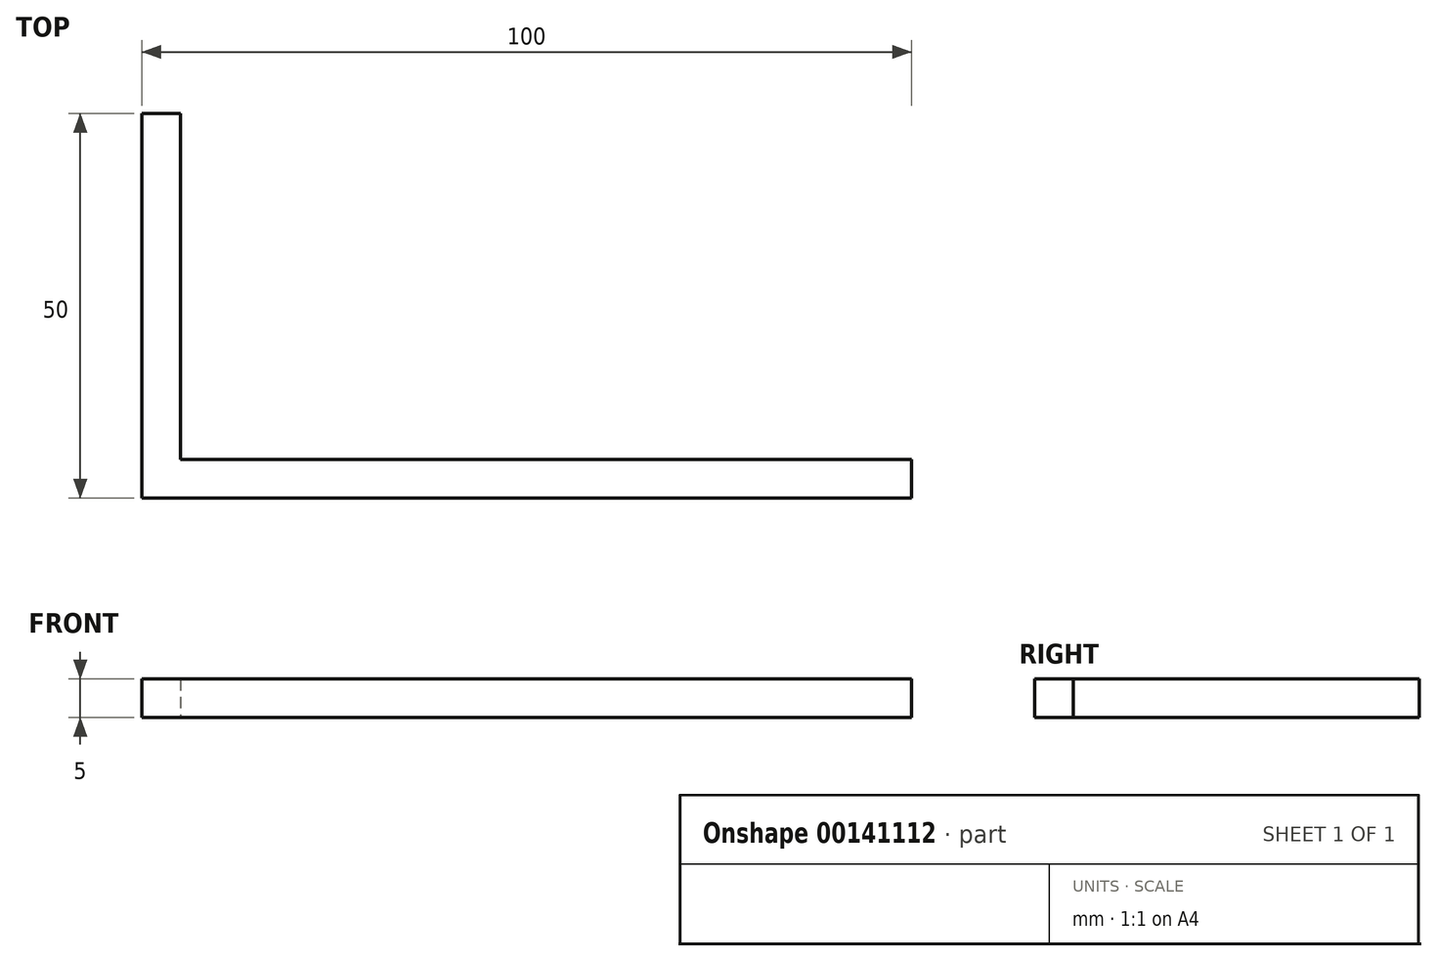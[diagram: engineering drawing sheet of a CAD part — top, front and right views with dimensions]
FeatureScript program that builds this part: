
annotation { "Feature Type Name" : "Feature", "Feature Type Description" : "" }
export const myFeature = defineFeature(function(context is Context, id is Id, definition is map)
    precondition{}
    {
        {
            var Q0;
            Q0=qCreatedBy(makeId("Top.planeOp"),FACE);
            var sketch = newSketch(context, id + "F0", { "sketchPlane" : qUnion([Q0])});
            skLineSegment(sketch, "E0.bottom", {"start": v(50, -2.5) * mm, "end": v(-50, -2.5) * mm});
            skLineSegment(sketch, "E0.top", {"start": v(50, 2.5) * mm, "end": v(-50, 2.5) * mm});
            skLineSegment(sketch, "E0.left", {"start": v(50, -2.5) * mm, "end": v(50, 2.5) * mm});
            skLineSegment(sketch, "E0.right", {"start": v(-50, -2.5) * mm, "end": v(-50, 2.5) * mm});
            skPoint(sketch, "E0.middle", {"position": v(0, 0) * mm});
            skLineSegment(sketch, "E1", {"start": v(-50, 2.5) * mm, "end": v(-50, 47.5) * mm});
            skLineSegment(sketch, "E2", {"start": v(-50, 47.5) * mm, "end": v(-45, 47.5) * mm});
            skLineSegment(sketch, "E3", {"start": v(-45, 47.5) * mm, "end": v(-45, 2.5) * mm});
            skLineSegment(sketch, "E4", {"start": v(-45, 47.5) * mm, "end": v(-45, 42.5) * mm});
            skLineSegment(sketch, "E5", {"start": v(-45, 42.5) * mm, "end": v(-50, 42.5) * mm});
            skLineSegment(sketch, "E6", {"start": v(-50, 42.5) * mm, "end": v(-50, 47.5) * mm});
            skLineSegment(sketch, "E7", {"start": v(-45, 2.5) * mm, "end": v(-45, -2.5) * mm});
            skLineSegment(sketch, "E8", {"start": v(-5, 2.5) * mm, "end": v(-5, -2.5) * mm});
            skLineSegment(sketch, "E9", {"start": v(-5, -2.5) * mm, "end": v(0, -2.5) * mm});
            skLineSegment(sketch, "E10", {"start": v(0, -2.5) * mm, "end": v(0, 2.5) * mm});
            skLineSegment(sketch, "E11", {"start": v(45, 2.5) * mm, "end": v(45, -2.5) * mm});
            skLineSegment(sketch, "E12", {"start": v(45, -2.5) * mm, "end": v(50, -2.5) * mm});
            skSolve(sketch);
        }
        {
            var Q0;
            Q0=makeQuery(id+"F0.imprint","IMPRINT",FACE,{"disambiguationData":[TD([[makeQuery(id+"F0.imprint","IMPRINT",EDGE,{"derivedFrom":sQuery(id+"F0.wireOp",EDGE,"E2")}),-1.0]])]});
            var Q1;
            {var subQ0=sQuery(id+"F0.wireOp",EDGE,"E0.right");Q1=makeQuery(id+"F0.imprint","IMPRINT",FACE,{"disambiguationData":[TD([[makeQuery(id+"F0.imprint","IMPRINT",EDGE,{"derivedFrom":subQ0}),-1.0]])]});}
            var Q2;
            {var subQ0=sQuery(id+"F0.wireOp",EDGE,"E8");Q2=makeQuery(id+"F0.imprint","IMPRINT",FACE,{"disambiguationData":[TD([[makeQuery(id+"F0.imprint","IMPRINT",EDGE,{"derivedFrom":subQ0}),1.0]])]});}
            var Q3;
            {var subQ0=sQuery(id+"F0.wireOp",EDGE,"E0.left");Q3=makeQuery(id+"F0.imprint","IMPRINT",FACE,{"disambiguationData":[TD([[makeQuery(id+"F0.imprint","IMPRINT",EDGE,{"derivedFrom":subQ0}),1.0]])]});}
            extrude(context, id + "F1", {"entities" : qUnion([Q0, Q1, Q2, Q3]), "depth" : 5 * mm});
        }
        {
            var Q0;
            Q0 = qSketchRegion(id + "F0", true);
            extrude(context, id + "F2", {"entities" : qUnion([Q0]), "operationType" : NewBodyOperationType.ADD, "depth" : 1 * mm});
        }
        {
            var Q0;
            Q0 = qSketchRegion(id + "F0", true);
            extrude(context, id + "F3", {"entities" : qUnion([Q0]), "depth" : 5 * mm});
        }
    });
